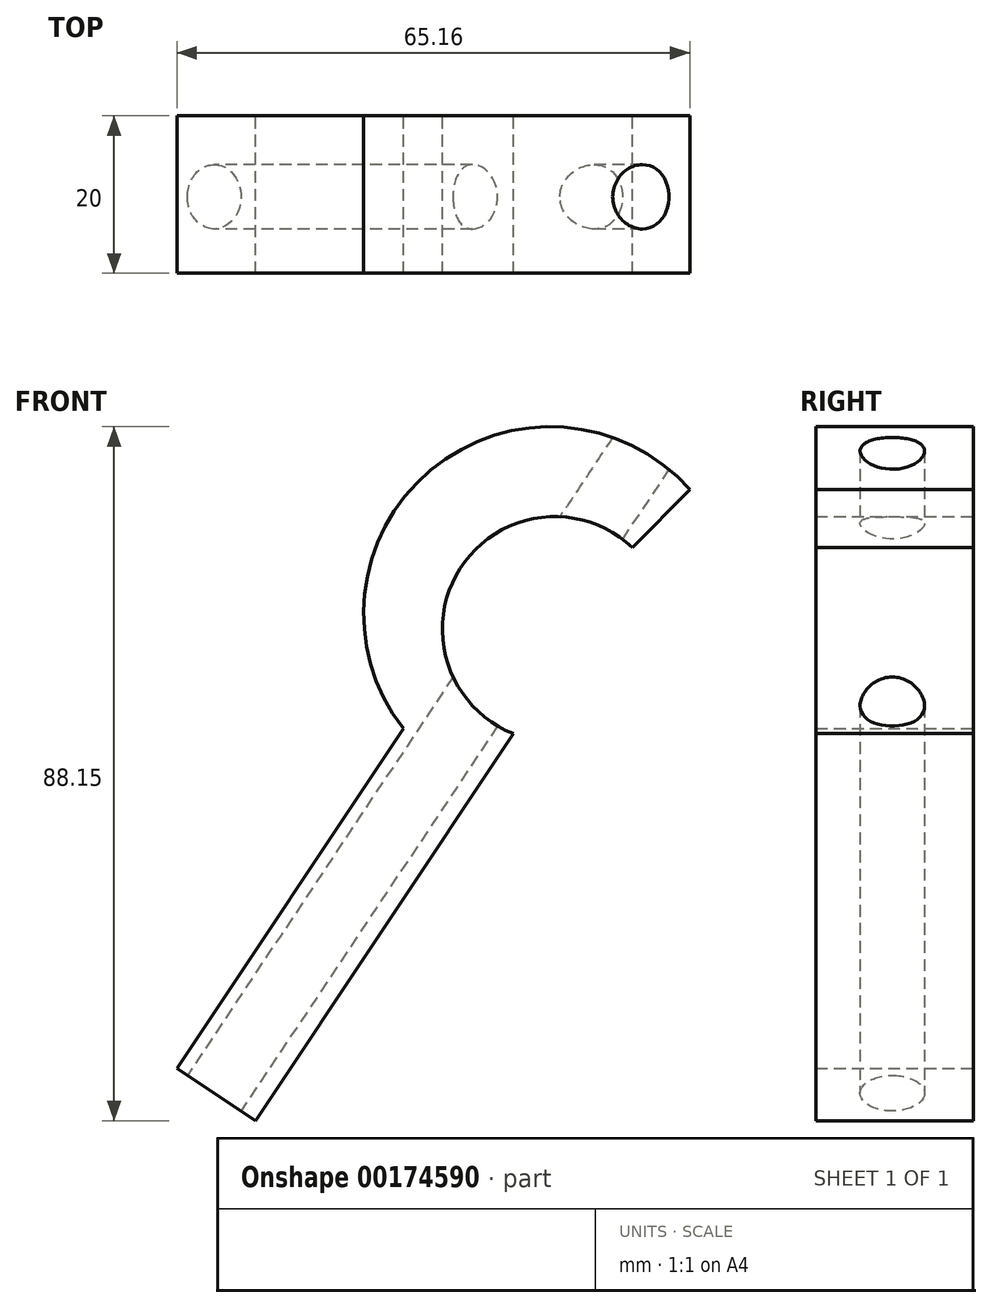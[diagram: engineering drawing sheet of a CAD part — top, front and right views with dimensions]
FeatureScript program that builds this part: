
annotation { "Feature Type Name" : "Feature", "Feature Type Description" : "" }
export const myFeature = defineFeature(function(context is Context, id is Id, definition is map)
    precondition{}
    {
        {
            var Q0;
            Q0=qCreatedBy(makeId("Front.planeOp"),FACE);
            var sketch = newSketch(context, id + "F0", { "sketchPlane" : qUnion([Q0])});
            skLineSegment(sketch, "E0", {"start": v(-11.05, 30.2) * mm, "end": v(-39.83, -12.96) * mm});
            skLineSegment(sketch, "E1", {"start": v(-39.83, -12.96) * mm, "end": v(-29.86, -19.6) * mm});
            skArc(sketch, "E2", {"start": v(25.33, 60.59) * mm, "mid": v(-7.6, 63.04) * mm, "end": v(-11.05, 30.2) * mm});
            skLineSegment(sketch, "E3", {"start": v(-29.86, -19.6) * mm, "end": v(2.91, 29.56) * mm});
            skArc(sketch, "E4", {"start": v(18.04, 53.2) * mm, "mid": v(-3.85, 50.55) * mm, "end": v(2.91, 29.56) * mm});
            skLineSegment(sketch, "E5", {"start": v(18.04, 53.2) * mm, "end": v(25.33, 60.59) * mm});
            skSolve(sketch);
        }
        {
            var Q0;
            Q0=makeQuery(id+"F0.imprint","IMPRINT",FACE,{"disambiguationData":[TD([[makeQuery(id+"F0.imprint","IMPRINT",EDGE,{"derivedFrom":sQuery(id+"F0.wireOp",EDGE,"E0")}),1.0]])]});
            extrude(context, id + "F1", {"entities" : qUnion([Q0]), "depth" : 20 * mm});
        }
        {
            var Q0;
            Q0=makeQuery(id+"F1.opExtrude","SWEPT_FACE",FACE,{"disambiguationData":[OSD([sQuery(id+"F0.wireOp",EDGE,"E1")])]});
            var sketch = newSketch(context, id + "F2", { "sketchPlane" : qUnion([Q0])});
            skCircle(sketch, "E6", {"center": v(-20.26, 10.29) * mm, "radius": 4.09 * mm});
            skSolve(sketch);
        }
        {
            var Q0;
            Q0=makeQuery(id+"F2.imprint","IMPRINT",FACE,{"disambiguationData":[TD([[makeQuery(id+"F2.imprint","IMPRINT",EDGE,{"derivedFrom":sQuery(id+"F2.wireOp",EDGE,"E6")}),1.0]])]});
            extrude(context, id + "F3", {"entities" : qUnion([Q0]), "operationType" : NewBodyOperationType.REMOVE, "endBound" : BoundingType.THROUGH_ALL, "oppositeDirection" : true, "depth" : 25 * mm});
        }
    });
